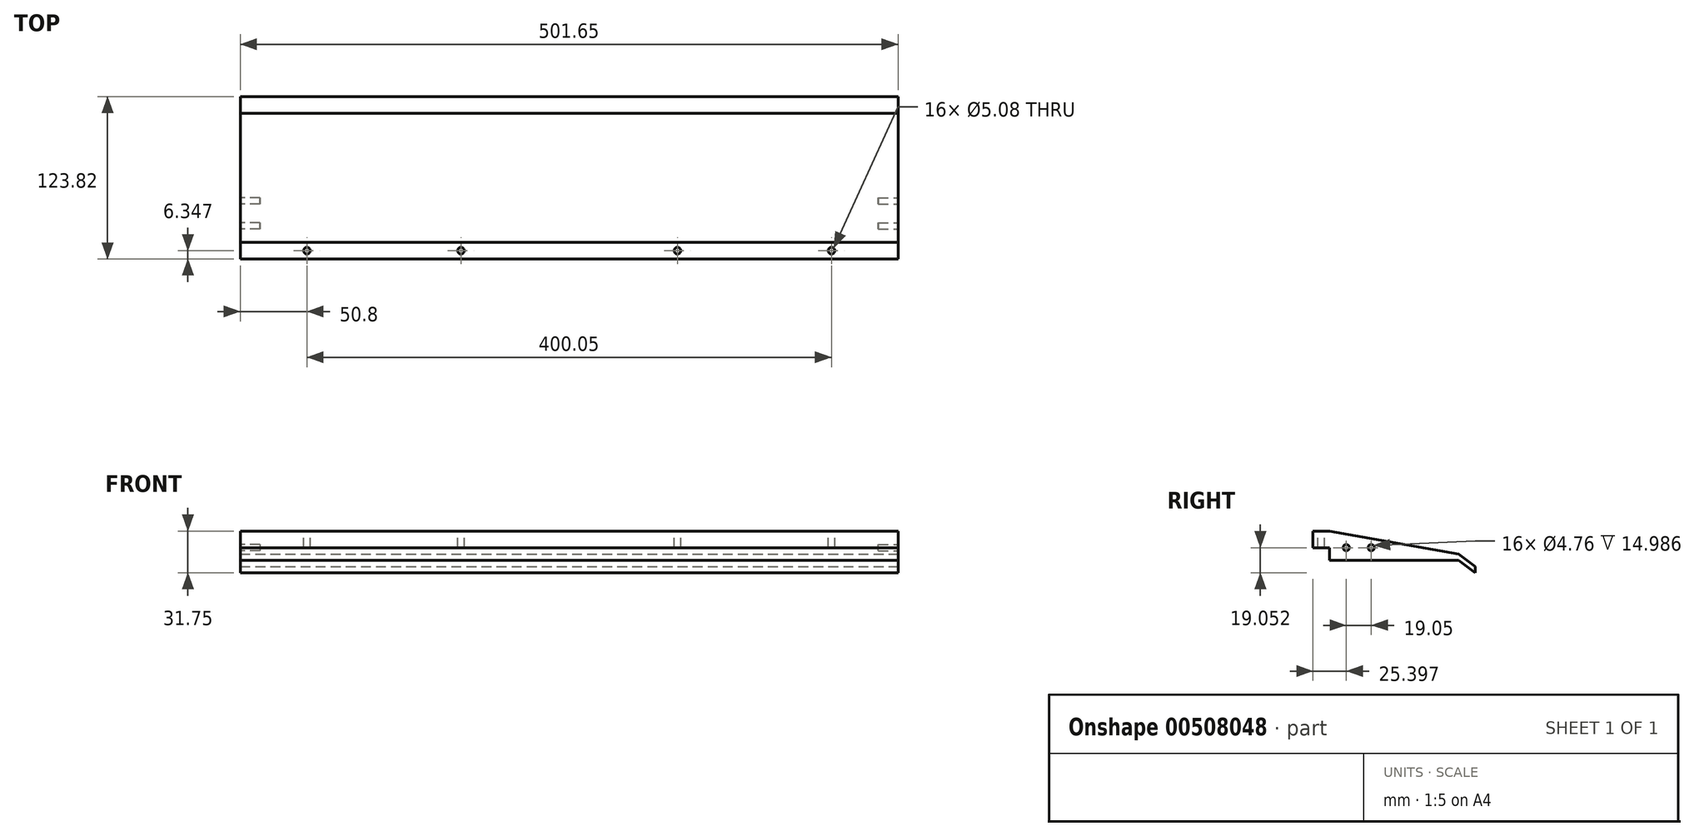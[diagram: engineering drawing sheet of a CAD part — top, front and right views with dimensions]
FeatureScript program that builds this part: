
annotation { "Feature Type Name" : "Feature", "Feature Type Description" : "" }
export const myFeature = defineFeature(function(context is Context, id is Id, definition is map)
    precondition{}
    {
        {
            var Q0;
            Q0=qCreatedBy(makeId("Right.planeOp"),FACE);
            var sketch = newSketch(context, id + "F0", { "sketchPlane" : qUnion([Q0])});
            skLineSegment(sketch, "E0", {"start": v(-52.27, 38.91) * mm, "end": v(-39.57, 38.91) * mm});
            skLineSegment(sketch, "E1", {"start": v(-39.57, 38.91) * mm, "end": v(58.85, 21.44) * mm});
            skLineSegment(sketch, "E2", {"start": v(58.85, 21.44) * mm, "end": v(71.55, 11.91) * mm});
            skLineSegment(sketch, "E3", {"start": v(71.55, 11.91) * mm, "end": v(71.55, 7.16) * mm});
            skLineSegment(sketch, "E4", {"start": v(71.55, 7.16) * mm, "end": v(58.85, 16.69) * mm});
            skLineSegment(sketch, "E5", {"start": v(58.85, 16.69) * mm, "end": v(-39.57, 16.69) * mm});
            skLineSegment(sketch, "E6", {"start": v(-39.57, 16.69) * mm, "end": v(-39.57, 26.21) * mm});
            skLineSegment(sketch, "E7", {"start": v(-39.57, 26.21) * mm, "end": v(-52.27, 26.21) * mm});
            skLineSegment(sketch, "E8", {"start": v(-52.27, 26.21) * mm, "end": v(-52.27, 38.91) * mm});
            skSolve(sketch);
        }
        {
            var Q0;
            Q0 = qSketchRegion(id + "F0", true);
            extrude(context, id + "F1", {"entities" : qUnion([Q0]), "oppositeDirection" : true, "depth" : 501.65 * mm, "offsetDistance" : 25.4 * mm});
        }
        {
            var Q0;
            Q0=makeQuery(id+"F1.opExtrude","CAP_FACE",FACE,{"disambiguationData":[OSD([sQuery(id+"F0.wireOp",EDGE,"E0"),sQuery(id+"F0.wireOp",EDGE,"E1"),sQuery(id+"F0.wireOp",EDGE,"E2"),sQuery(id+"F0.wireOp",EDGE,"E3"),sQuery(id+"F0.wireOp",EDGE,"E4"),sQuery(id+"F0.wireOp",EDGE,"E5"),sQuery(id+"F0.wireOp",EDGE,"E6"),sQuery(id+"F0.wireOp",EDGE,"E7"),sQuery(id+"F0.wireOp",EDGE,"E8")])],"isStart":true});
            var sketch = newSketch(context, id + "F2", { "sketchPlane" : qUnion([Q0])});
            skPoint(sketch, "E9", {"position": v(-26.87, 26.21) * mm});
            skPoint(sketch, "E10", {"position": v(-7.82, 26.21) * mm});
            skCircle(sketch, "E11", {"center": v(-26.87, 26.21) * mm, "radius": 2.38 * mm});
            skCircle(sketch, "E12", {"center": v(-7.82, 26.21) * mm, "radius": 2.38 * mm});
            skSolve(sketch);
        }
        {
            var Q0;
            Q0 = qSketchRegion(id + "F2", true);
            extrude(context, id + "F3", {"entities" : qUnion([Q0]), "operationType" : NewBodyOperationType.REMOVE, "oppositeDirection" : true, "depth" : 15 * mm});
        }
        {
            var Q0;
            Q0=makeQuery(id+"F1.opExtrude","CAP_FACE",FACE,{"disambiguationData":[OSD([sQuery(id+"F0.wireOp",EDGE,"E0"),sQuery(id+"F0.wireOp",EDGE,"E1"),sQuery(id+"F0.wireOp",EDGE,"E2"),sQuery(id+"F0.wireOp",EDGE,"E3"),sQuery(id+"F0.wireOp",EDGE,"E4"),sQuery(id+"F0.wireOp",EDGE,"E5"),sQuery(id+"F0.wireOp",EDGE,"E6"),sQuery(id+"F0.wireOp",EDGE,"E7"),sQuery(id+"F0.wireOp",EDGE,"E8")])],"isStart":false});
            var sketch = newSketch(context, id + "F4", { "sketchPlane" : qUnion([Q0])});
            skCircle(sketch, "E13", {"center": v(26.87, 26.21) * mm, "radius": 2.38 * mm});
            skCircle(sketch, "E14", {"center": v(7.82, 26.21) * mm, "radius": 2.38 * mm});
            skSolve(sketch);
        }
        {
            var Q0;
            Q0 = qSketchRegion(id + "F4", true);
            extrude(context, id + "F5", {"entities" : qUnion([Q0]), "operationType" : NewBodyOperationType.REMOVE, "oppositeDirection" : true, "depth" : 15 * mm});
        }
        {
            var Q0;
            Q0=makeQuery(id+"F1.opExtrude","SWEPT_FACE",FACE,{"disambiguationData":[OSD([sQuery(id+"F0.wireOp",EDGE,"E0")])]});
            var sketch = newSketch(context, id + "F6", { "sketchPlane" : qUnion([Q0])});
            skCircle(sketch, "E15", {"center": v(-450.85, -45.92) * mm, "radius": 2.54 * mm});
            skCircle(sketch, "E16", {"center": v(-333.38, -45.92) * mm, "radius": 2.54 * mm});
            skCircle(sketch, "E17", {"center": v(-168.28, -45.92) * mm, "radius": 2.54 * mm});
            skCircle(sketch, "E18", {"center": v(-50.8, -45.92) * mm, "radius": 2.54 * mm});
            skSolve(sketch);
        }
        {
            var Q0;
            Q0 = qSketchRegion(id + "F6", true);
            extrude(context, id + "F7", {"entities" : qUnion([Q0]), "operationType" : NewBodyOperationType.REMOVE, "endBound" : BoundingType.THROUGH_ALL, "oppositeDirection" : true, "depth" : 25.4 * mm});
        }
    });
